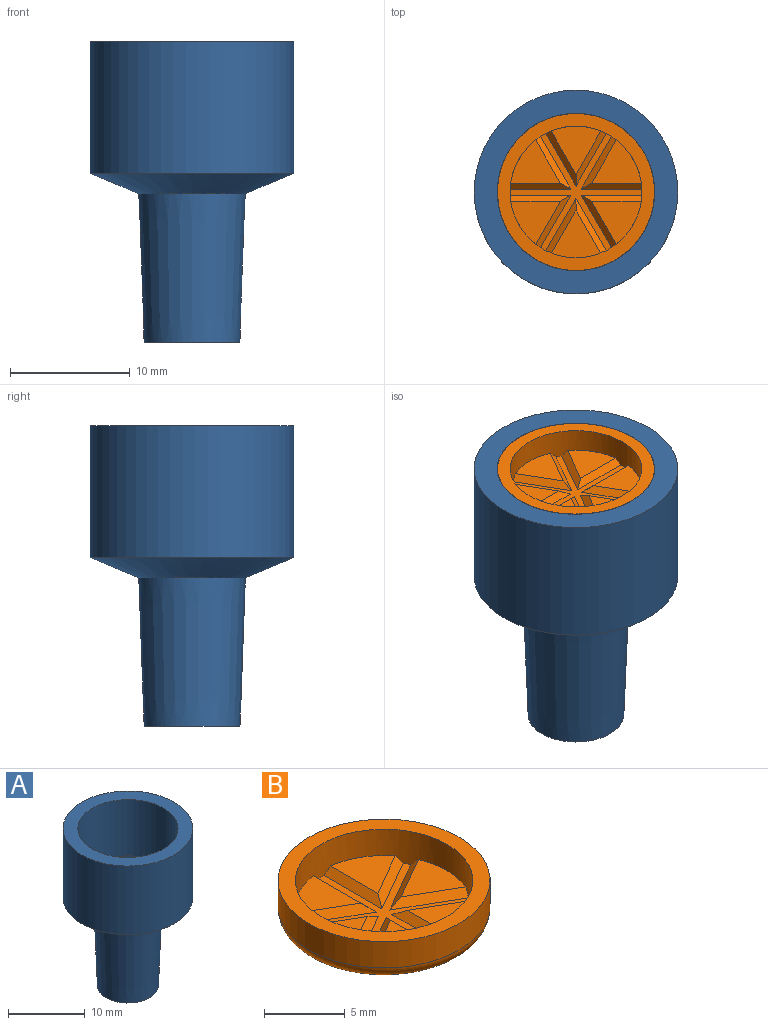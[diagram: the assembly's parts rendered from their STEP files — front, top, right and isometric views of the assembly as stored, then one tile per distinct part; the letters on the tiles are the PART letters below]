
ASSEMBLY  parts=2 mates=1
PART A: 14 faces, bbox 17x17x25.1 mm
  f0: plane 9.1x9.1mm, normal (0,0,1), area 36.8mm2, adj f1,f11
  f1: cylinder r=3mm len=8mm, axis (0,0,-1), area 150.8mm2, adj f0,f2
  f2: plane 6x6mm, normal (0,0,1), area 24.3mm2, adj f1,f12,f13
  f3: plane 6x6mm, normal (0,0,-1), area 24.3mm2, adj f4,f12,f13
  f4: cylinder r=3mm len=6mm, axis (0,0,-1), area 28.3mm2, adj f3,f5
  f5: plane 8x8mm, normal (0,0,-1), area 22mm2, adj f4,f6
  f6: cone r=4mm half-angle=2.1deg, axis (0,0,1), area 329.4mm2, adj f5,f7
  f7: cone r=4.45mm half-angle=67.2deg, axis (0,0,1), area 178.7mm2, adj f6,f8
  f8: cylinder r=8.5mm len=17mm, axis (0,0,-1), area 587.5mm2, adj f7,f9
  f9: plane 17x17mm, normal (0,0,1), area 92.2mm2, adj f8,f10
  f10: cylinder r=6.55mm len=13.1mm, axis (0,0,-1), area 370.4mm2, adj f9,f11
  f11: torus R=4.55mm, axis (0,0,-1), area 114.9mm2, adj f0,f10
  f12: cylinder r=0.8mm len=4.6mm, axis (0,0,-1), area 23.1mm2, adj f2,f3
  f13: cylinder r=0.8mm len=4.6mm, axis (0,0,-1), area 23.1mm2, adj f2,f3
PART B: 24 faces, bbox 14.2x14.2x3 mm
  f0: plane 4.15x3.59mm, normal (0,0,1), area 8.6mm2, adj f8,f18,f19
  f1: plane 4.15x4mm, normal (0,0,1), area 8.6mm2, adj f8,f16,f17
  f2: plane 4.15x3.59mm, normal (0,0,1), area 8.6mm2, adj f8,f14,f15
  f3: plane 4.15x4mm, normal (0,0,1), area 8.6mm2, adj f8,f20,f21
  f4: plane 4.15x3.59mm, normal (0,0,1), area 8.6mm2, adj f8,f22,f23
  f5: cylinder r=6.58mm len=13.15mm, axis (0,0,-1), area 82.6mm2, adj f6,f10
  f6: plane 13.15x13.15mm, normal (0,0,1), area 40.8mm2, adj f5,f8
  f7: plane 11.15x11.15mm, normal (0,0,-1), area 97.6mm2, adj f10
  f8: cylinder r=5.5mm len=11mm, axis (0,0,1), area 72.1mm2, adj f0,f1,f2,f3,f4,f6,f9,f11
  f9: plane 4.15x3.59mm, normal (0,0,1), area 8.6mm2, adj f8,f12,f13
  f10: torus R=5.58mm, axis (0,0,1), area 61.3mm2, adj f5,f7
  f11: plane 11x9.77mm, normal (0,0,1), area 15.8mm2, adj f8,f12,f13,f14,f15,f16,f17,f18
  f12: plane 5.06x0.5mm, normal (-0.71,0,0.71), area 3.3mm2, adj f8,f9,f11,f13
  f13: plane 4.38x2.94mm, normal (0.35,0.61,0.71), area 3.3mm2, adj f8,f9,f11,f12
  f14: plane 5.06x0.5mm, normal (0.71,0,0.71), area 3.3mm2, adj f2,f8,f11,f15
  f15: plane 4.38x2.94mm, normal (-0.35,0.61,0.71), area 3.3mm2, adj f2,f8,f11,f14
  f16: plane 4.59x2.53mm, normal (0.35,-0.61,0.71), area 3.3mm2, adj f1,f8,f11,f17
  f17: plane 4.59x2.53mm, normal (0.35,0.61,0.71), area 3.3mm2, adj f1,f8,f11,f16
  f18: plane 4.38x2.94mm, normal (-0.35,-0.61,0.71), area 3.3mm2, adj f0,f8,f11,f19
  f19: plane 5.06x0.5mm, normal (0.71,0,0.71), area 3.3mm2, adj f0,f8,f11,f18
  f20: plane 4.59x2.53mm, normal (-0.35,-0.61,0.71), area 3.3mm2, adj f3,f8,f11,f21
  f21: plane 4.59x2.53mm, normal (-0.35,0.61,0.71), area 3.3mm2, adj f3,f8,f11,f20
  f22: plane 4.38x2.94mm, normal (0.35,-0.61,0.71), area 3.3mm2, adj f4,f8,f11,f23
  f23: plane 5.06x0.5mm, normal (-0.71,0,0.71), area 3.3mm2, adj f4,f8,f11,f22
PLACE A rot(axis=(0,0,-1),90deg) t=(0,0,0)mm
PLACE B rot(axis=(0,0,-1),90deg) t=(0,0,-3)mm
MATE cylindrical B.f5 <-> A.f1  axis (0,0,1) through (0,0,25.1)mm
